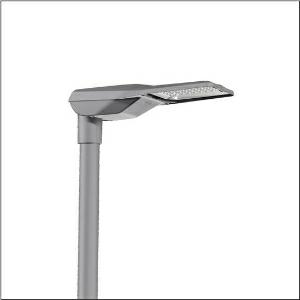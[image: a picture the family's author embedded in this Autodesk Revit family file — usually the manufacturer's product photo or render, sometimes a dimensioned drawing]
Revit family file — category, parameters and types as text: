
# Revit family: streetlight_sl_21_iq_mini___st1_0a_5xe2d31d08gb_54bd
name_source: partatom
category: Lighting Fixtures
units: mm (PartAtom-declared; Revit-internal decimal feet)

## family parameters
Cut with Voids When Loaded = No
Host = Face
Light Source = No
Part Type = Normal
Room Calculation Point = No
Round Connector Dimension = Use Diameter
Shared = No

## types (1)
- --- (1 x LED, 5680 lm, 37.1 W, 3000K)
    Apparent Load = 37 VA
    CIE Flux Codes = 37 72 97 100 100
    Color Rendering = 70
    Color Temperature = 3000K
    Default Elevation = 1800 mm
    Description = Streetlight SL 21 iQ mini, mast luminaire, primary light control with lens, of PMMA, primary optical cover: cover, of toughened safety glass, transparent, light distribution: ST1.0a, light emission: direct distribution, primary light characteristic: asymmetric, installation type: post-top, side-entry, LED, High Power LED, rated luminous flux: 5.680lm, luminous efficacy: 153lm/W, light colour: 730, colour temperature: 3000K, control gear: iQ-Comfort, control: Auto-Match, Temp-Guard, Lumen-Switch, Night-Set, Smart-Wire, Light-Fading, Desk-Remote (wireless, voltage-free reading and setting of iQ features in the workshop via application-optimized NFC function/RFID function), optimised constant luminous flux control (CLO 2.0), pre-setting: linear dimming characteristic, mains connection: 220..240V, AC, 50/60Hz, start of lifetime: 37W, end of service life: 39W, reduction: 18W, luminaire housing, of diecast aluminium, powder-coated, Siteco® metallic grey (DB 702S), corrosivity category C5 mid according to DIN EN ISO 12944, please order mast flange separately, inclination adjustable: 0°, 5°, 10°, 15°, sealing non-destructively replaceable, multi-level sealing system, length: 628mm, width: 235mm, height: 110mm, mast flange for spigot size: 42mm (side-entry): 5XC10008XM4, 60/48mm (side-entry/post-top): 5XC10108XM2, 76/60mm (side-entry/post-top): 5XC10108XM1, mounting height: 4..8m, protection rating (complete): IP66, insulation class (complete): insulation class II (safety insulation), certification: CE, ENEC, ENEC+, VDE, impact resistance: IK10, permissible operating ambient temperature for outdoor applications: -40..+50°C, standard-compliant lighting for roads and squares, packaging unit: 1 piece

Light Distribution: ST1.0a
    Height = 110 mm
    Lamp = 1 x LED
    Lamp Light Flux = 5680 lm
    Lamp Power = 37.1 W
    Lamp count = 1
    Length = 625 mm
    Luminous efficacy = 153 lm/W
    Manufacturer = Siteco
    ModVariant = No
    Model = 5XE2D31D08GB
    Number of Poles = 1
    OnlyDefault = Yes
    Power Factor = 1
    Product Name = Streetlight SL 21 iQ mini | ST1.0a
    Product group = mast luminaire | pylon top
    ProductGroupID = 6100
    Protection Class = Protection class II
    Protection Degree = IP 66
    RLX_Detail_Level = 1
    RLX_Emergency_Light_Flux = 0 lm
    RLX_Emergency_Type = 0
    RLX_Emergency_Type_DB = No
    RlxData = <blob elided: 26345 chars, md5=96f638a2>
    Socket = socket
    Standby Power = 0 W
    System Light Flux = 5680 lm
    System Power = 37 W
    Type Comments = factory setting: luminous flux: 100 % | dim-lin: 254 | 385 mA
    Type Image = l_1003519.jpg
    URL = http://relux.com
    VarID = @adj_188954
    Voltage = 0 V
    Weight = 0.00 kg
    Width = 234 mm

## geometry (parser evidence)
native form markers: Blend x4, Sweep x13
no freeform markers — native parametric forms only
